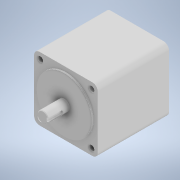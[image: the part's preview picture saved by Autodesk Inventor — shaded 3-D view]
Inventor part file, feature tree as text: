
AUTODESK INVENTOR PART (.ipt)
format: ipt  version: 2022 (Build 260153000, 153)  size: 164,352 bytes
history: native  units: in
note: dims shown in document units (in); Inventor stores cm internally (conversion verified against a paired STEP export)
features: extrude x5, sketch x5, fillet x2, chamfer x1
ambient origin geometry x8: Origin, YZ Plane, XZ Plane, XY Plane, X Axis, Y Axis, Z Axis, Center Point
bodies: Solid1 (feature_tree)
feature tree (13):
  extrude  "Extrusion1"  Depth=4.3307in
  extrude  "Extrusion2"  Depth=4.9213in
  extrude  "Extrusion3"  Depth=0.374in
  extrude  "Extrusion4"  Depth=0.1181in TaperAngle=0.0deg
  fillet  "Fillet1"  Radius=3.7402in
  chamfer  "Chamfer1"  Distance=0.1181in
  extrude  "Extrusion5"  Depth=0.1181in TaperAngle=0.0deg
  fillet  "Fillet2"  Radius=0.374in
  sketch  "Sketch1"  dims[d0=4.3307in d1=4.3307in]
  sketch  "Sketch2"  dims[d2=4.8425in d3=0.0in d4=4.9213in]
  sketch  "Sketch3"  dims[d5=45.0deg d6=0.374in]
  sketch  "Sketch4"  dims[d7=1.5748in d9=360.0deg d11=4.8425in d12=0.0in d13=3.7402in d14=0.1181in d15=0.0in]
  sketch  "Sketch5"  dims[d16=0.748in d17=1.4567in d18=0.0in d19=0.374in d20=0.0394in d21=0.0787in d22=45.0deg d23=0.2362in d24=0.2362in d25=0.0in d26=0.8819in d27=0.9843in d28=0.0in d29=0.1181in]
